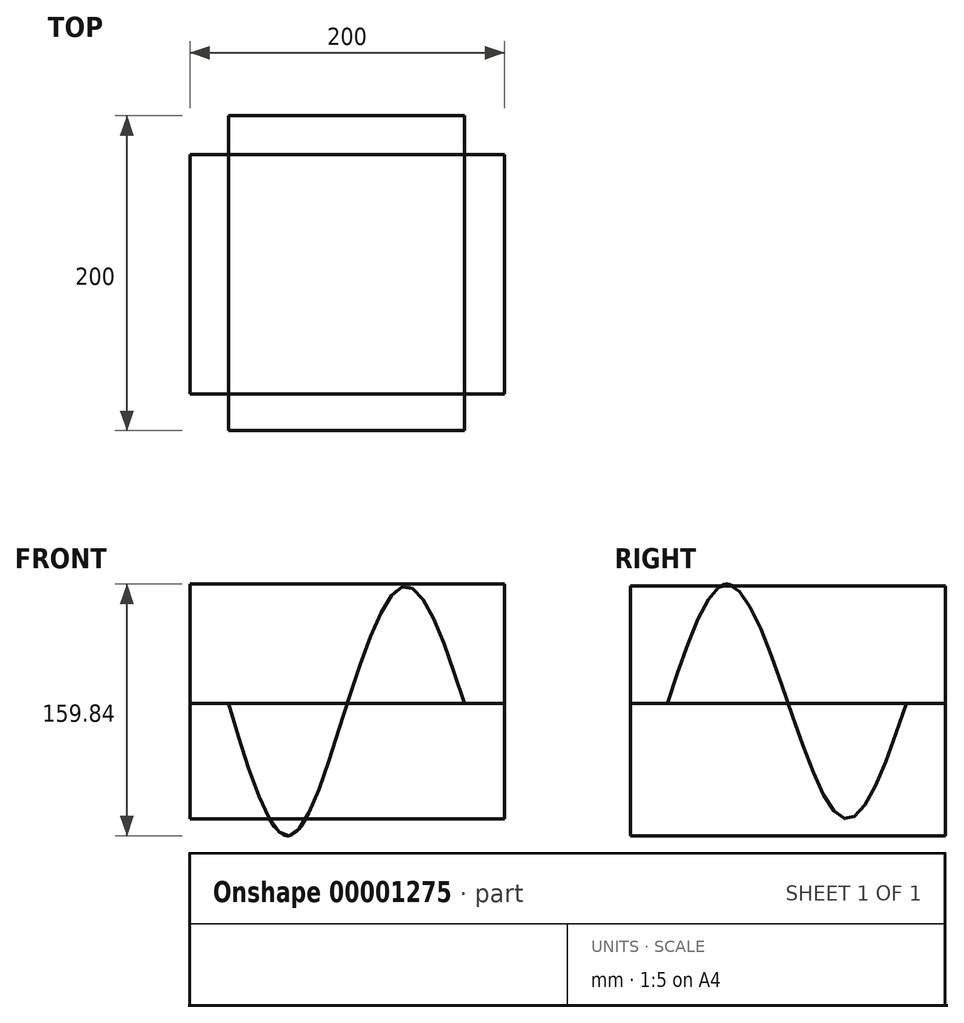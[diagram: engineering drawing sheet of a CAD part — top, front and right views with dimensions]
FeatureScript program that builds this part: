
annotation { "Feature Type Name" : "Feature", "Feature Type Description" : "" }
export const myFeature = defineFeature(function(context is Context, id is Id, definition is map)
    precondition{}
    {
        {
            var Q0;
            Q0=qCreatedBy(makeId("Right.planeOp"),FACE);
            var sketch = newSketch(context, id + "F0", { "sketchPlane" : qUnion([Q0])});
            skLineSegment(sketch, "E0", {"start": v(-76.66, 0) * mm, "end": v(0, 0) * mm});
            skLineSegment(sketch, "E1", {"start": v(0, 0) * mm, "end": v(75.2, 0) * mm});
            skLineSegment(sketch, "E2", {"start": v(0, 0) * mm, "end": v(0, 75.86) * mm});
            skLineSegment(sketch, "E3", {"start": v(0, 75.86) * mm, "end": v(-77.94, 75.86) * mm, "construction": true});
            skLineSegment(sketch, "E4", {"start": v(0, 0) * mm, "end": v(0, -73.26) * mm, "construction": true});
            skLineSegment(sketch, "E5", {"start": v(0, -73.26) * mm, "end": v(75.18, -73.26) * mm, "construction": true});
            skFitSpline(sketch, "E6", {"points": [v(75.2, 0) * mm, v(37.6, -73.26) * mm, v(0, 0) * mm, v(-38.97, 75.86) * mm, v(-76.66, 0) * mm], "startDerivative": vector(-151.95, -442.47) * mm, "endDerivative": vector(-148.4, -452.45) * mm});
            skSolve(sketch);
        }
        {
            var Q0;
            {var subQ1=sQuery(id+"F0.wireOp",EDGE,"E0");Q0=makeQuery(id+"F0.imprint","IMPRINT",FACE,{"disambiguationData":[TD([[makeQuery(id+"F0.imprint","IMPRINT",EDGE,{"derivedFrom":subQ1}),1.0]])]});}
            var Q1;
            {var subQ1=sQuery(id+"F0.wireOp",EDGE,"E1");Q1=makeQuery(id+"F0.imprint","IMPRINT",FACE,{"disambiguationData":[TD([[makeQuery(id+"F0.imprint","IMPRINT",EDGE,{"derivedFrom":subQ1}),-1.0]])]});}
            var Q2;
            Q2=sQuery(id+"F0.wireOp",EDGE,"E6");
            extrude(context, id + "F1", {"entities" : qUnion([Q0, Q1]), "bodyType" : ToolBodyType.SURFACE, "surfaceEntities" : qUnion([Q2]), "oppositeDirection" : true, "depth" : 200 * mm, "symmetric" : true});
        }
        {
            var Q0;
            Q0=qCreatedBy(makeId("Front.planeOp"),FACE);
            var sketch = newSketch(context, id + "F2", { "sketchPlane" : qUnion([Q0])});
            skLineSegment(sketch, "E7", {"start": v(0, 0) * mm, "end": v(-75.4, 0) * mm});
            skLineSegment(sketch, "E8", {"start": v(74.57, 0) * mm, "end": v(0, 0) * mm});
            skLineSegment(sketch, "E9", {"start": v(37.28, 0) * mm, "end": v(37.28, 74.6) * mm});
            skLineSegment(sketch, "E10", {"start": v(-37.7, 0) * mm, "end": v(-37.7, -83.97) * mm, "construction": true});
            skFitSpline(sketch, "E11", {"points": [v(74.57, 0) * mm, v(37.28, 74.6) * mm, v(0, 0) * mm, v(-37.7, -83.97) * mm, v(-75.4, 0) * mm], "startDerivative": vector(-152.5, 456.64) * mm, "endDerivative": vector(-147.6, 494.11) * mm});
            skSolve(sketch);
        }
        {
            var Q0;
            Q0=sQuery(id+"F2.wireOp",EDGE,"E11");
            extrude(context, id + "F3", {"bodyType" : ToolBodyType.SURFACE, "surfaceEntities" : qUnion([Q0]), "depth" : 200 * mm, "symmetric" : true});
        }
    });
